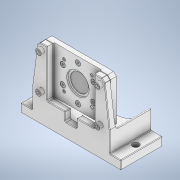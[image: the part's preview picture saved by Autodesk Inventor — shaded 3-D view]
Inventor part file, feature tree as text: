
AUTODESK INVENTOR PART (.ipt)
format: ipt  version: 2021 (Build 250183000, 183)  size: 503,808 bytes
history: native  units: mm
features: extrude x1, sketch x1
ambient origin geometry x8: Origin, YZ Plane, XZ Plane, XY Plane, X Axis, Y Axis, Z Axis, Center Point
bodies: Solid1 (feature_tree), Volumenkörper1 (feature_tree)
feature tree (2):
  extrude  "Extrusion1"  [1 undecoded]
  sketch  "Sketch1"  dims[d0=50.0mm d1=0.0mm]
note: 1 required parameter value undecoded (feature->parameter linkage not recoverable at this tier; creation-order binding heuristic only, values carry confidence <= 0.55)
